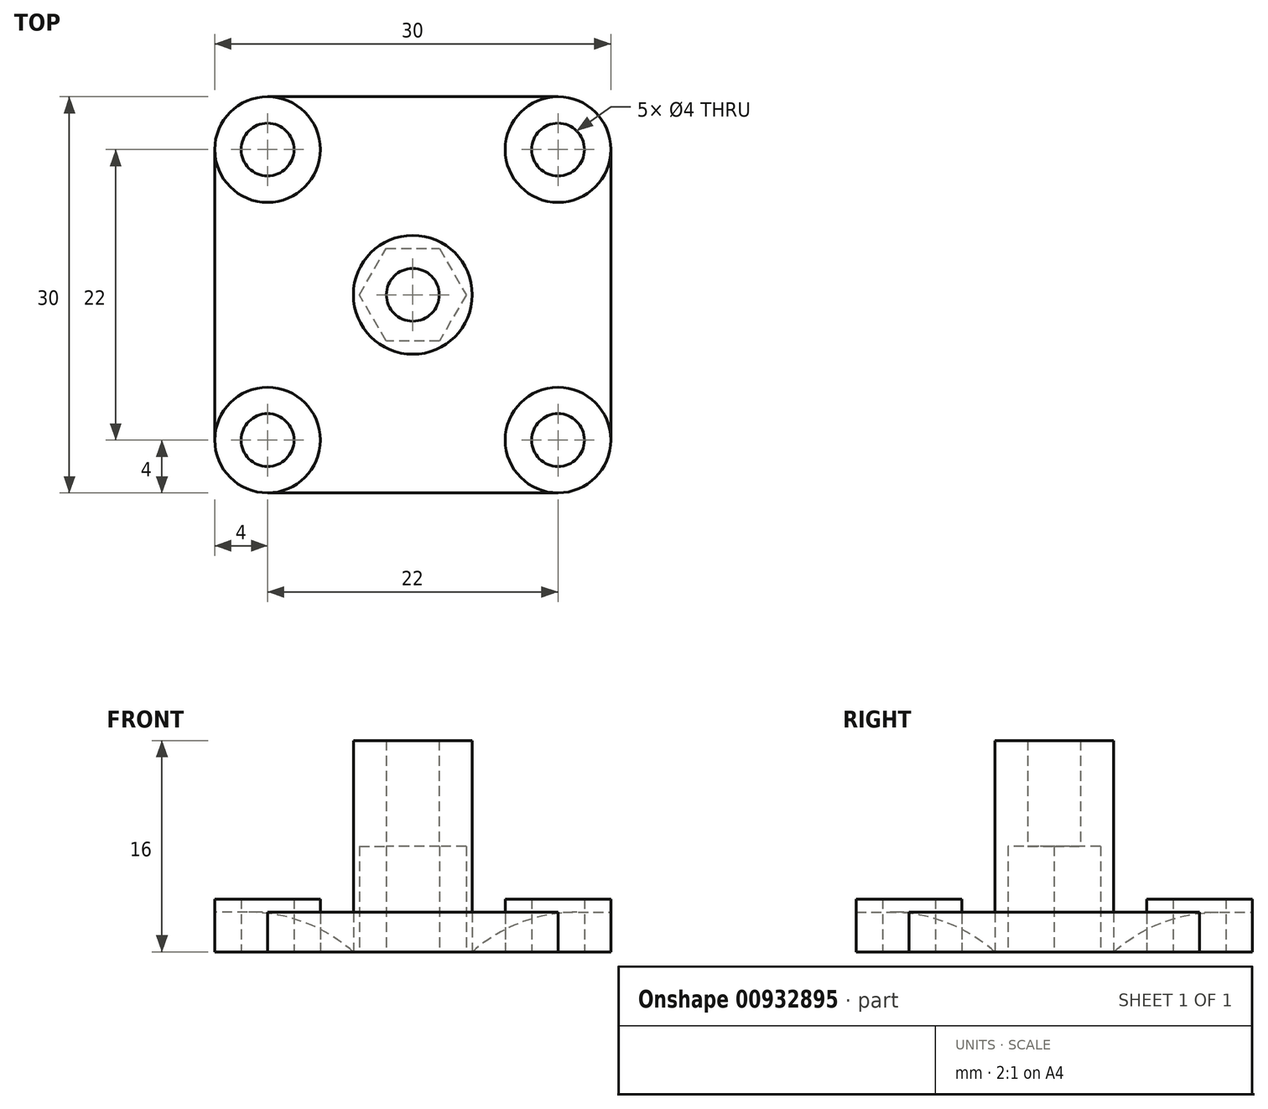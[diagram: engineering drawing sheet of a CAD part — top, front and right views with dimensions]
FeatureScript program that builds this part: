
annotation { "Feature Type Name" : "Feature", "Feature Type Description" : "" }
export const myFeature = defineFeature(function(context is Context, id is Id, definition is map)
    precondition{}
    {
        {
            var Q0;
            Q0=qCreatedBy(makeId("Top.planeOp"),FACE);
            var sketch = newSketch(context, id + "F0", { "sketchPlane" : qUnion([Q0])});
            skLineSegment(sketch, "E0.bottom", {"start": v(-11, 15) * mm, "end": v(11, 15) * mm});
            skLineSegment(sketch, "E0.top", {"start": v(-11, -15) * mm, "end": v(11, -15) * mm});
            skLineSegment(sketch, "E0.left", {"start": v(-15, 11) * mm, "end": v(-15, -11) * mm});
            skLineSegment(sketch, "E0.right", {"start": v(15, 11) * mm, "end": v(15, -11) * mm});
            skPoint(sketch, "E0.middle", {"position": v(0, 0) * mm});
            skPoint(sketch, "E1.visualSharp", {"position": v(15, -15) * mm});
            skArc(sketch, "E1.filletArc", {"start": v(11, -15) * mm, "mid": v(13.83, -13.83) * mm, "end": v(15, -11) * mm});
            skPoint(sketch, "E2.visualSharp", {"position": v(-15, -15) * mm});
            skArc(sketch, "E2.filletArc", {"start": v(-15, -11) * mm, "mid": v(-13.83, -13.83) * mm, "end": v(-11, -15) * mm});
            skPoint(sketch, "E3.visualSharp", {"position": v(-15, 15) * mm});
            skArc(sketch, "E3.filletArc", {"start": v(-11, 15) * mm, "mid": v(-13.83, 13.83) * mm, "end": v(-15, 11) * mm});
            skPoint(sketch, "E4.visualSharp", {"position": v(15, 15) * mm});
            skArc(sketch, "E4.filletArc", {"start": v(15, 11) * mm, "mid": v(13.83, 13.83) * mm, "end": v(11, 15) * mm});
            skCircle(sketch, "E5", {"center": v(0, 0) * mm, "radius": 2 * mm});
            skCircle(sketch, "E6", {"center": v(0, 0) * mm, "radius": 4.5 * mm});
            skCircle(sketch, "E7", {"center": v(11, 11) * mm, "radius": 2 * mm});
            skCircle(sketch, "E8", {"center": v(11, -11) * mm, "radius": 2 * mm});
            skCircle(sketch, "E9", {"center": v(-11, -11) * mm, "radius": 2 * mm});
            skCircle(sketch, "E10", {"center": v(-11, 11) * mm, "radius": 2 * mm});
            skCircle(sketch, "E11", {"center": v(11, 11) * mm, "radius": 4 * mm});
            skCircle(sketch, "E12", {"center": v(-11, 11) * mm, "radius": 4 * mm});
            skCircle(sketch, "E13", {"center": v(-11, -11) * mm, "radius": 4 * mm});
            skCircle(sketch, "E14", {"center": v(11, -11) * mm, "radius": 4 * mm});
            skSolve(sketch);
        }
        {
            var Q0;
            Q0=makeQuery(id+"F0.imprint","IMPRINT",FACE,{"disambiguationData":[TD([[makeQuery(id+"F0.imprint","IMPRINT",EDGE,{"derivedFrom":sQuery(id+"F0.wireOp",EDGE,"E10")}),-1.0]])]});
            var Q1;
            Q1=makeQuery(id+"F0.imprint","IMPRINT",FACE,{"disambiguationData":[TD([[makeQuery(id+"F0.imprint","IMPRINT",EDGE,{"derivedFrom":sQuery(id+"F0.wireOp",EDGE,"E7")}),-1.0]])]});
            var Q2;
            Q2=makeQuery(id+"F0.imprint","IMPRINT",FACE,{"disambiguationData":[TD([[makeQuery(id+"F0.imprint","IMPRINT",EDGE,{"derivedFrom":sQuery(id+"F0.wireOp",EDGE,"E8")}),-1.0]])]});
            var Q3;
            Q3=makeQuery(id+"F0.imprint","IMPRINT",FACE,{"disambiguationData":[TD([[makeQuery(id+"F0.imprint","IMPRINT",EDGE,{"derivedFrom":sQuery(id+"F0.wireOp",EDGE,"E9")}),-1.0]])]});
            extrude(context, id + "F1", {"entities" : qUnion([Q0, Q1, Q2, Q3]), "depth" : 4 * mm, "offsetDistance" : 25 * mm});
        }
        {
            var Q0;
            Q0=makeQuery(id+"F0.imprint","IMPRINT",FACE,{"disambiguationData":[TD([[makeQuery(id+"F0.imprint","IMPRINT",EDGE,{"derivedFrom":sQuery(id+"F0.wireOp",EDGE,"E5")}),-1.0]])]});
            extrude(context, id + "F2", {"entities" : qUnion([Q0]), "depth" : 16 * mm, "offsetDistance" : 25 * mm});
        }
        {
            var Q0;
            {var subQ3=sQuery(id+"F0.wireOp",EDGE,"E0.bottom");Q0=makeQuery(id+"F0.imprint","IMPRINT",FACE,{"disambiguationData":[TD([[makeQuery(id+"F0.imprint","IMPRINT",EDGE,{"derivedFrom":subQ3}),-1.0]])]});}
            extrude(context, id + "F3", {"entities" : qUnion([Q0]), "depth" : 3 * mm, "offsetDistance" : 25 * mm});
        }
        {
            var Q0;
            Q0=makeQuery(id+"F3.opExtrude","CAP_EDGE",EDGE,{"disambiguationData":[OSD([sQuery(id+"F0.wireOp",EDGE,"E6")])],"isStart":false});
            fillet(context, id + "F4", {"entities" : qUnion([Q0]), "radius" : 12 * mm, "tangentPropagation" : true, "allowEdgeOverflow" : false});
        }
        {
            var Q0;
            {var subQ3=sQuery(id+"F0.wireOp",EDGE,"E0.bottom");Q0=makeQuery(id+"F0.imprint","IMPRINT",FACE,{"disambiguationData":[TD([[makeQuery(id+"F0.imprint","IMPRINT",EDGE,{"derivedFrom":subQ3}),-1.0]])]});}
            var sketch = newSketch(context, id + "F5", { "sketchPlane" : qUnion([Q0])});
            skCircle(sketch, "E15.cCircle", {"center": v(0, 0) * mm, "radius": 3.5 * mm, "construction": true});
            skLineSegment(sketch, "E15.0", {"start": v(2.02, -3.5) * mm, "end": v(-2.02, -3.5) * mm});
            skLineSegment(sketch, "E15.1", {"start": v(-2.02, -3.5) * mm, "end": v(-4.04, 0) * mm});
            skLineSegment(sketch, "E15.2", {"start": v(-4.04, 0) * mm, "end": v(-2.02, 3.5) * mm});
            skLineSegment(sketch, "E15.3", {"start": v(-2.02, 3.5) * mm, "end": v(2.02, 3.5) * mm});
            skLineSegment(sketch, "E15.4", {"start": v(2.02, 3.5) * mm, "end": v(4.04, 0) * mm});
            skLineSegment(sketch, "E15.5", {"start": v(4.04, 0) * mm, "end": v(2.02, -3.5) * mm});
            skPoint(sketch, "E15.0.midPoint", {"position": v(0, -3.5) * mm});
            skSolve(sketch);
        }
        {
            var Q0;
            Q0 = qSketchRegion(id + "F5", true);
            extrude(context, id + "F6", {"entities" : qUnion([Q0]), "operationType" : NewBodyOperationType.REMOVE, "depth" : 8 * mm, "offsetDistance" : 25 * mm});
        }
    });
